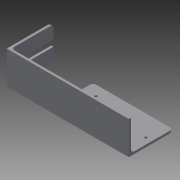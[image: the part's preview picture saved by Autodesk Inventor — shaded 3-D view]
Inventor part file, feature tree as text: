
AUTODESK INVENTOR PART (.ipt)
format: ipt  version: 2015 (Build 190159000, 159)  size: 153,600 bytes
history: native  units: mm
features: extrude x3, sketch x3, hole x2, fillet x1
ambient origin geometry x8: Origin, YZ Plane, XZ Plane, XY Plane, X Axis, Y Axis, Z Axis, Center Point
bodies: Solid1 (feature_tree)
feature tree (9):
  extrude  "Main Mount"  Depth=54.5mm
  extrude  "Base"  Depth=13.25mm
  extrude  "Laser Mount"  Depth=4.0mm
  hole  "Cable Management"  [1 undecoded]
  hole  "Cable Routing"  [1 undecoded]
  fillet  "Strength"  Radius=8.0mm
  sketch  "Sketch1"  dims[d0=104.0mm d1=54.5mm]
  sketch  "Sketch2"  dims[d9=28.0mm d10=13.25mm]
  sketch  "Sketch3"  dims[d11=17.0mm d12=3.25mm d13=3.25mm d14=17.0mm d15=8.0mm d16=3.25mm d17=27.25mm d18=3.0mm d19=0.0mm d20=55.0mm d21=43.0mm d22=3.0mm d23=0.0mm d24=3.0mm d31=8.0mm d32=55.0mm d33=0.0mm d34=10.0mm d35=10.0mm d46=5.0mm d47=5.0mm d48=6.5mm d49=6.0mm d50=4.0mm d51=2.0mm d52=90.0deg d53=8.0mm d54=20.594885mm d55=5.0mm d56=5.0mm d57=4.0mm d58=6.0mm d59=4.0mm d60=2.0mm d61=90.0deg d62=8.0mm d63=20.594885mm d64=4.0mm d65=1.0mm]
note: 2 required parameter values undecoded (feature->parameter linkage not recoverable at this tier; creation-order binding heuristic only, values carry confidence <= 0.55)
